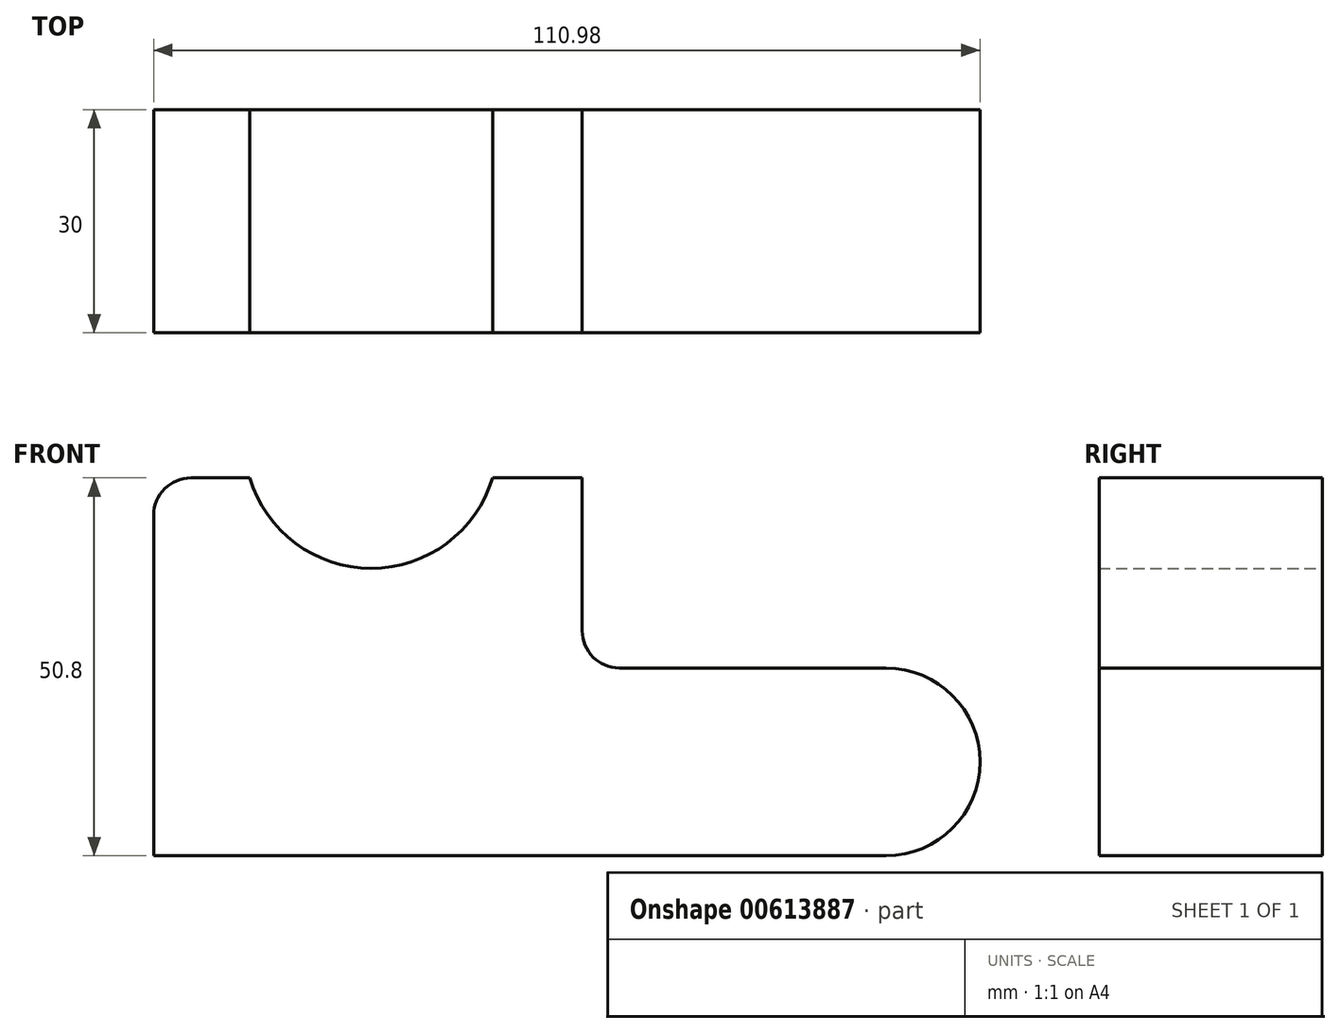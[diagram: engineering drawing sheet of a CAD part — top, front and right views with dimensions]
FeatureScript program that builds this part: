
annotation { "Feature Type Name" : "Feature", "Feature Type Description" : "" }
export const myFeature = defineFeature(function(context is Context, id is Id, definition is map)
    precondition{}
    {
        {
            var Q0;
            Q0=qCreatedBy(makeId("Front.planeOp"),FACE);
            var sketch = newSketch(context, id + "F0", { "sketchPlane" : qUnion([Q0])});
            skLineSegment(sketch, "E0.bottom", {"start": v(-58.27, 21.73) * mm, "end": v(-50.35, 21.73) * mm});
            skLineSegment(sketch, "E0.top", {"start": v(-63.27, -29.07) * mm, "end": v(-5.73, -29.07) * mm});
            skLineSegment(sketch, "E0.left", {"start": v(-63.27, 16.73) * mm, "end": v(-63.27, -29.07) * mm});
            skLineSegment(sketch, "E0.right", {"start": v(-5.73, 21.73) * mm, "end": v(-5.73, 1.18) * mm});
            skArc(sketch, "E1", {"start": v(-50.35, 21.73) * mm, "mid": v(-34.06, 9.57) * mm, "end": v(-17.76, 21.73) * mm});
            skLineSegment(sketch, "E2.trimOffspring", {"start": v(-17.76, 21.73) * mm, "end": v(-5.73, 21.73) * mm});
            skPoint(sketch, "E3.visualSharp", {"position": v(-63.27, 21.73) * mm});
            skArc(sketch, "E3.filletArc", {"start": v(-58.27, 21.73) * mm, "mid": v(-61.8, 20.26) * mm, "end": v(-63.27, 16.73) * mm});
            skLineSegment(sketch, "E4.bottom", {"start": v(-5.73, -29.07) * mm, "end": v(35.09, -29.07) * mm});
            skLineSegment(sketch, "E4.top", {"start": v(-0.73, -3.82) * mm, "end": v(35.09, -3.82) * mm});
            skPoint(sketch, "E5.visualSharp", {"position": v(-5.73, -3.82) * mm});
            skArc(sketch, "E5.filletArc", {"start": v(-5.73, 1.18) * mm, "mid": v(-4.26, -2.35) * mm, "end": v(-0.73, -3.82) * mm});
            skArc(sketch, "E6", {"start": v(35.09, -29.07) * mm, "mid": v(47.71, -16.44) * mm, "end": v(35.09, -3.82) * mm});
            skSolve(sketch);
        }
        {
            var Q0;
            Q0 = qSketchRegion(id + "F0", true);
            extrude(context, id + "F1", {"entities" : qUnion([Q0]), "depth" : 30 * mm, "offsetDistance" : 25 * mm});
        }
    });
